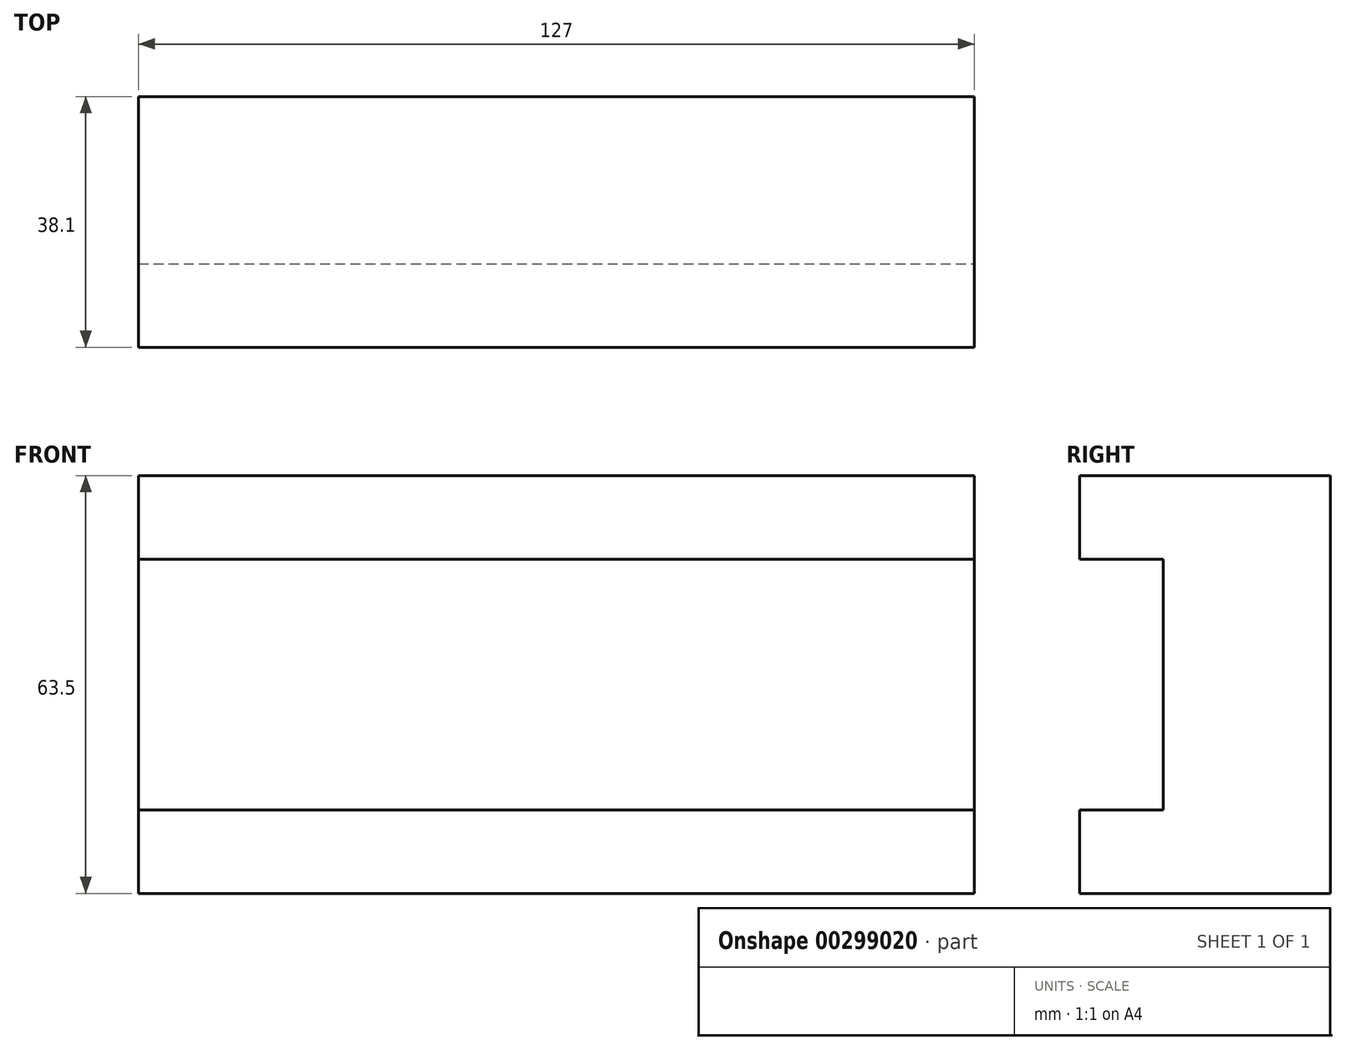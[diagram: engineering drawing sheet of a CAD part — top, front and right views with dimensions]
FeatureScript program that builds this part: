
annotation { "Feature Type Name" : "Feature", "Feature Type Description" : "" }
export const myFeature = defineFeature(function(context is Context, id is Id, definition is map)
    precondition{}
    {
        {
            var Q0;
            Q0=qCreatedBy(makeId("Front.planeOp"),FACE);
            var sketch = newSketch(context, id + "F0", { "sketchPlane" : qUnion([Q0])});
            skLineSegment(sketch, "E0.bottom", {"start": v(-63.5, 31.75) * mm, "end": v(63.5, 31.75) * mm});
            skLineSegment(sketch, "E0.top", {"start": v(-63.5, -31.75) * mm, "end": v(63.5, -31.75) * mm});
            skLineSegment(sketch, "E0.left", {"start": v(-63.5, 31.75) * mm, "end": v(-63.5, -31.75) * mm});
            skLineSegment(sketch, "E0.right", {"start": v(63.5, 31.75) * mm, "end": v(63.5, -31.75) * mm});
            skPoint(sketch, "E0.middle", {"position": v(0, 0) * mm});
            skSolve(sketch);
        }
        {
            var Q0;
            Q0=makeQuery(id+"F0.imprint","IMPRINT",FACE,{"disambiguationData":[TD([[makeQuery(id+"F0.imprint","IMPRINT",EDGE,{"derivedFrom":sQuery(id+"F0.wireOp",EDGE,"E0.bottom")}),-1.0]])]});
            extrude(context, id + "F1", {"entities" : qUnion([Q0]), "depth" : 38.1 * mm});
        }
        {
            var Q0;
            Q0=makeQuery(id+"F1.opExtrude","CAP_FACE",FACE,{"disambiguationData":[OSD([sQuery(id+"F0.wireOp",EDGE,"E0.bottom"),sQuery(id+"F0.wireOp",EDGE,"E0.top"),sQuery(id+"F0.wireOp",EDGE,"E0.left"),sQuery(id+"F0.wireOp",EDGE,"E0.right")])],"isStart":false});
            var sketch = newSketch(context, id + "F2", { "sketchPlane" : qUnion([Q0])});
            skLineSegment(sketch, "E1.bottom", {"start": v(-63.5, 19.05) * mm, "end": v(63.5, 19.05) * mm});
            skLineSegment(sketch, "E1.top", {"start": v(-63.5, -19.05) * mm, "end": v(63.5, -19.05) * mm});
            skLineSegment(sketch, "E1.left", {"start": v(-63.5, 19.05) * mm, "end": v(-63.5, -19.05) * mm});
            skLineSegment(sketch, "E1.right", {"start": v(63.5, 19.05) * mm, "end": v(63.5, -19.05) * mm});
            skPoint(sketch, "E1.middle", {"position": v(0, 0) * mm});
            skSolve(sketch);
        }
        {
            var Q0;
            Q0=makeQuery(id+"F2.imprint","IMPRINT",FACE,{"disambiguationData":[TD([[makeQuery(id+"F2.imprint","IMPRINT",EDGE,{"derivedFrom":sQuery(id+"F2.wireOp",EDGE,"E1.bottom")}),-1.0]])]});
            extrude(context, id + "F3", {"entities" : qUnion([Q0]), "operationType" : NewBodyOperationType.REMOVE, "oppositeDirection" : true, "depth" : 12.7 * mm});
        }
    });
